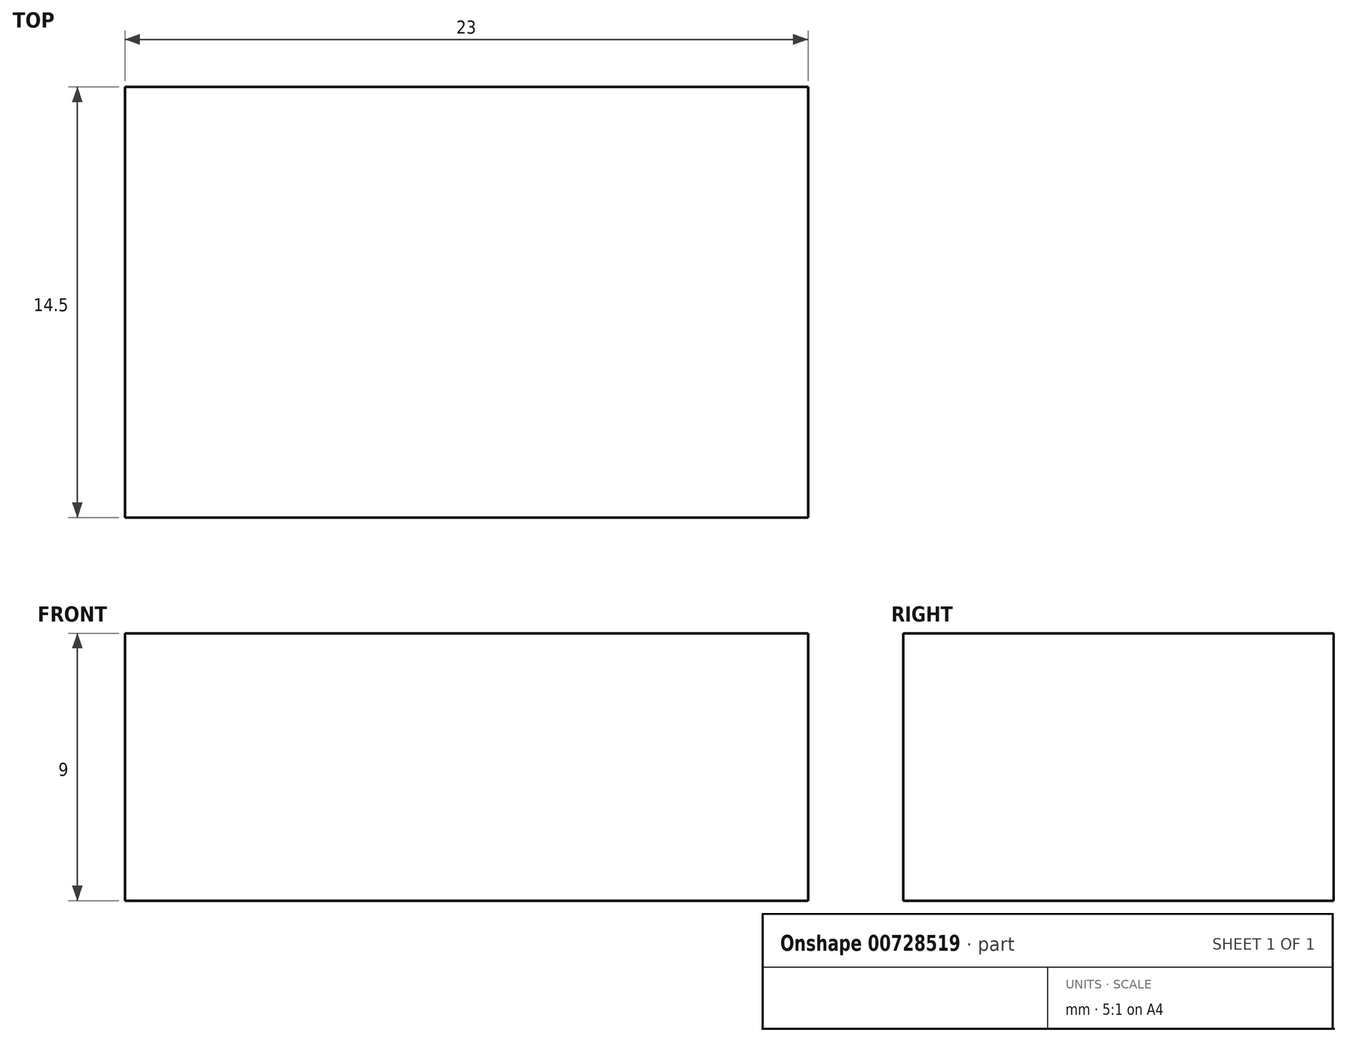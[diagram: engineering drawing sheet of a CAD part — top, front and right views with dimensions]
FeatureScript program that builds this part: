
annotation { "Feature Type Name" : "Feature", "Feature Type Description" : "" }
export const myFeature = defineFeature(function(context is Context, id is Id, definition is map)
    precondition{}
    {
        {
            var Q0;
            Q0=qCreatedBy(makeId("Top.planeOp"),FACE);
            var sketch = newSketch(context, id + "F0", { "sketchPlane" : qUnion([Q0])});
            skLineSegment(sketch, "E0.bottom", {"start": v(-23, 0) * mm, "end": v(0, 0) * mm});
            skLineSegment(sketch, "E0.top", {"start": v(-23, 14.5) * mm, "end": v(0, 14.5) * mm});
            skLineSegment(sketch, "E0.left", {"start": v(-23, 0) * mm, "end": v(-23, 14.5) * mm});
            skLineSegment(sketch, "E0.right", {"start": v(0, 0) * mm, "end": v(0, 14.5) * mm});
            skSolve(sketch);
        }
        {
            var Q0;
            Q0 = qSketchRegion(id + "F0", true);
            extrude(context, id + "F1", {"entities" : qUnion([Q0]), "depth" : 9 * mm, "offsetDistance" : 25 * mm});
        }
    });
